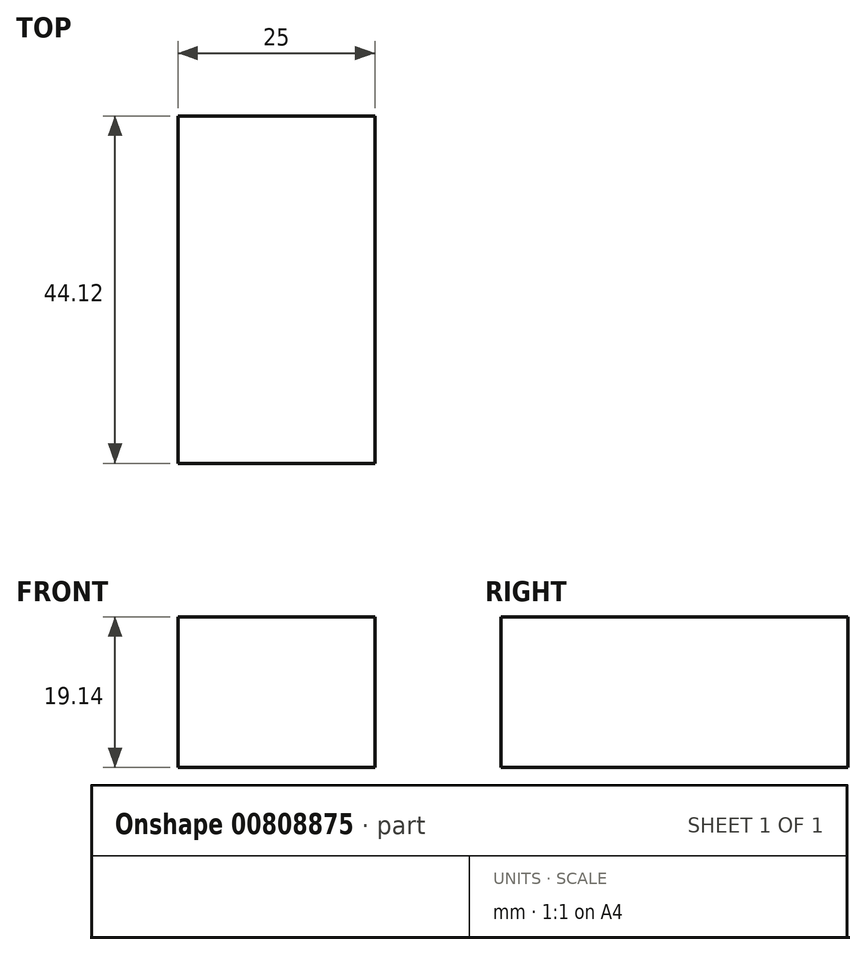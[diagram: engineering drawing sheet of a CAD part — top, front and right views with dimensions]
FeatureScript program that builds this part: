
annotation { "Feature Type Name" : "Feature", "Feature Type Description" : "" }
export const myFeature = defineFeature(function(context is Context, id is Id, definition is map)
    precondition{}
    {
        {
            var Q0;
            Q0=qCreatedBy(makeId("Top.planeOp"),FACE);
            var sketch = newSketch(context, id + "F0", { "sketchPlane" : qUnion([Q0])});
            skLineSegment(sketch, "E0.bottom", {"start": v(-37.89, 59.14) * mm, "end": v(37.89, 59.14) * mm});
            skLineSegment(sketch, "E0.top", {"start": v(-37.89, -59.14) * mm, "end": v(37.89, -59.14) * mm});
            skLineSegment(sketch, "E0.left", {"start": v(-37.89, 59.14) * mm, "end": v(-37.89, -59.14) * mm});
            skLineSegment(sketch, "E0.right", {"start": v(37.89, 59.14) * mm, "end": v(37.89, -59.14) * mm});
            skPoint(sketch, "E0.middle", {"position": v(0, 0) * mm});
            skSolve(sketch);
        }
        {
            var Q0;
            Q0=makeQuery(id+"F0.imprint","IMPRINT",FACE,{"disambiguationData":[TD([[makeQuery(id+"F0.imprint","IMPRINT",EDGE,{"derivedFrom":sQuery(id+"F0.wireOp",EDGE,"E0.bottom")}),-1.0]])]});
            extrude(context, id + "F1", {"entities" : qUnion([Q0]), "depth" : 62.6 * mm, "offsetDistance" : 25.4 * mm});
        }
        {
            var Q0;
            Q0=makeQuery(id+"F1.opExtrude","SWEPT_BODY",BODY,{"disambiguationData":[OSD([sQuery(id+"F0.wireOp",EDGE,"E0.bottom"),sQuery(id+"F0.wireOp",EDGE,"E0.top"),sQuery(id+"F0.wireOp",EDGE,"E0.left"),sQuery(id+"F0.wireOp",EDGE,"E0.right")])]});
            deleteBodies(context, id + "F2", {"entities" : qUnion([Q0])});
        }
        {
            var Q0;
            Q0=qCreatedBy(makeId("Right.planeOp"),FACE);
            var sketch = newSketch(context, id + "F3", { "sketchPlane" : qUnion([Q0])});
            skLineSegment(sketch, "E1.bottom", {"start": v(-22.06, 9.57) * mm, "end": v(22.06, 9.57) * mm});
            skLineSegment(sketch, "E1.top", {"start": v(-22.06, -9.57) * mm, "end": v(22.06, -9.57) * mm});
            skLineSegment(sketch, "E1.left", {"start": v(-22.06, 9.57) * mm, "end": v(-22.06, -9.57) * mm});
            skLineSegment(sketch, "E1.right", {"start": v(22.06, 9.57) * mm, "end": v(22.06, -9.57) * mm});
            skPoint(sketch, "E1.middle", {"position": v(0, 0) * mm});
            skSolve(sketch);
        }
        {
            var Q0;
            Q0 = qSketchRegion(id + "F3", true);
            extrude(context, id + "F4", {"entities" : qUnion([Q0]), "depth" : 25 * mm, "offsetDistance" : 25 * mm});
        }
    });
